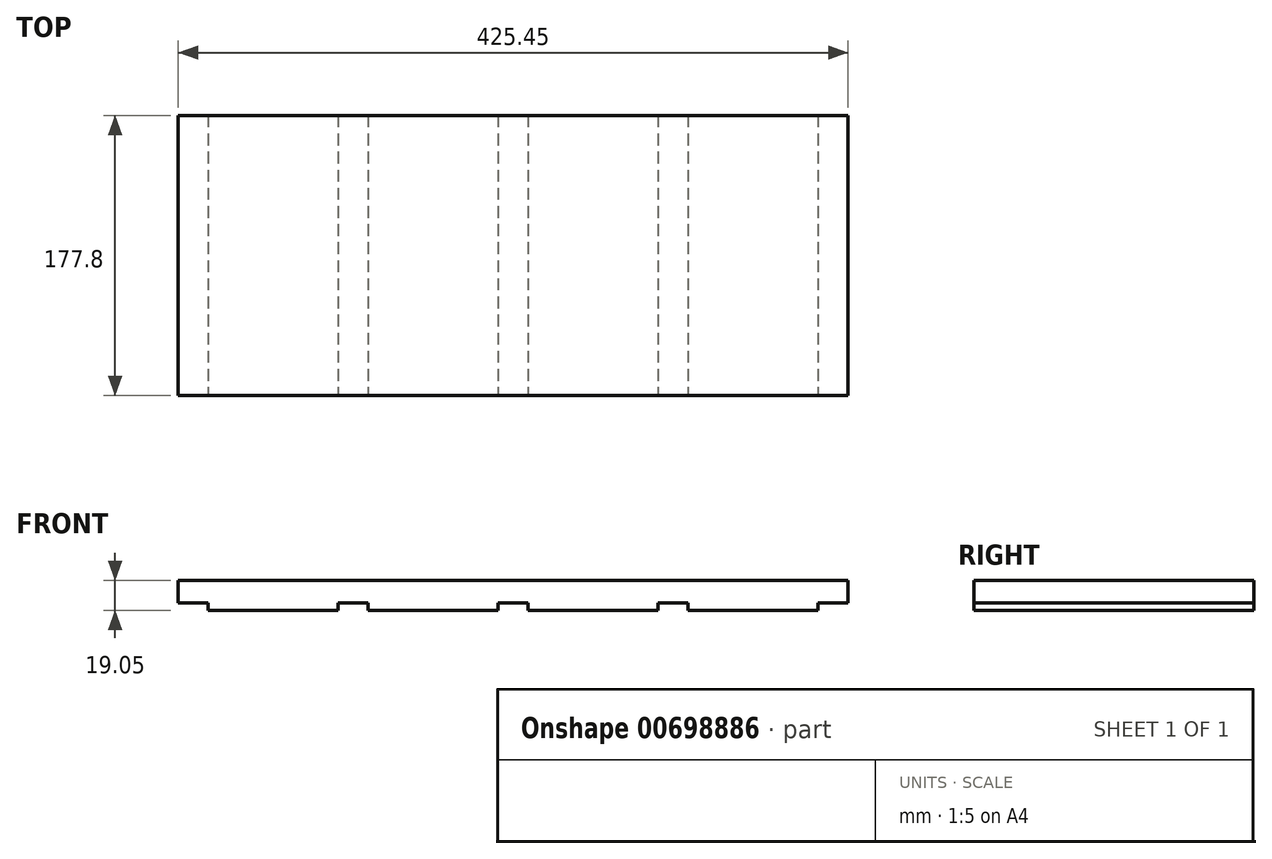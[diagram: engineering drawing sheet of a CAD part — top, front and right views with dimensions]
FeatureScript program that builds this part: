
annotation { "Feature Type Name" : "Feature", "Feature Type Description" : "" }
export const myFeature = defineFeature(function(context is Context, id is Id, definition is map)
    precondition{}
    {
        {
            var Q0;
            Q0=qCreatedBy(makeId("Front.planeOp"),FACE);
            var sketch = newSketch(context, id + "F0", { "sketchPlane" : qUnion([Q0])});
            skLineSegment(sketch, "E0.bottom", {"start": v(0, 0) * mm, "end": v(425.45, 0) * mm});
            skLineSegment(sketch, "E0.top", {"start": v(0, 19.05) * mm, "end": v(425.45, 19.05) * mm});
            skLineSegment(sketch, "E0.left", {"start": v(0, 0) * mm, "end": v(0, 19.05) * mm});
            skLineSegment(sketch, "E0.right", {"start": v(425.45, 0) * mm, "end": v(425.45, 19.05) * mm});
            skSolve(sketch);
        }
        {
            var Q0;
            Q0=qCreatedBy(makeId("Front.planeOp"),FACE);
            var sketch = newSketch(context, id + "F1", { "sketchPlane" : qUnion([Q0])});
            skLineSegment(sketch, "E1.bottom", {"start": v(101.6, 0) * mm, "end": v(120.65, 0) * mm});
            skLineSegment(sketch, "E1.top", {"start": v(101.6, 4.76) * mm, "end": v(120.65, 4.76) * mm});
            skLineSegment(sketch, "E1.left", {"start": v(101.6, 0) * mm, "end": v(101.6, 4.76) * mm});
            skLineSegment(sketch, "E1.right", {"start": v(120.65, 0) * mm, "end": v(120.65, 4.76) * mm});
            skLineSegment(sketch, "E2.1.0.0", {"start": v(203.2, 0) * mm, "end": v(222.25, 0) * mm});
            skLineSegment(sketch, "E2.1.0.1", {"start": v(203.2, 4.76) * mm, "end": v(222.25, 4.76) * mm});
            skLineSegment(sketch, "E2.1.0.2", {"start": v(203.2, 0) * mm, "end": v(203.2, 4.76) * mm});
            skLineSegment(sketch, "E2.1.0.3", {"start": v(222.25, 0) * mm, "end": v(222.25, 4.76) * mm});
            skLineSegment(sketch, "E2.2.0.0", {"start": v(304.8, 0) * mm, "end": v(323.85, 0) * mm});
            skLineSegment(sketch, "E2.2.0.1", {"start": v(304.8, 4.76) * mm, "end": v(323.85, 4.76) * mm});
            skLineSegment(sketch, "E2.2.0.2", {"start": v(304.8, 0) * mm, "end": v(304.8, 4.76) * mm});
            skLineSegment(sketch, "E2.2.0.3", {"start": v(323.85, 0) * mm, "end": v(323.85, 4.76) * mm});
            skLineSegment(sketch, "E2.direction1", {"start": v(101.6, 0) * mm, "end": v(203.2, 0) * mm, "construction": true});
            skLineSegment(sketch, "E3.0.3.0", {"start": v(406.4, 0) * mm, "end": v(425.45, 0) * mm});
            skLineSegment(sketch, "E3.3.3.0", {"start": v(406.4, 4.76) * mm, "end": v(425.45, 4.76) * mm});
            skLineSegment(sketch, "E3.6.3.0", {"start": v(406.4, 0) * mm, "end": v(406.4, 4.76) * mm});
            skLineSegment(sketch, "E3.9.3.0", {"start": v(425.45, 0) * mm, "end": v(425.45, 4.76) * mm});
            skLineSegment(sketch, "E4.bottom", {"start": v(0, 0) * mm, "end": v(19.05, 0) * mm});
            skLineSegment(sketch, "E4.top", {"start": v(0, 4.76) * mm, "end": v(19.05, 4.76) * mm});
            skLineSegment(sketch, "E4.left", {"start": v(0, 0) * mm, "end": v(0, 4.76) * mm});
            skLineSegment(sketch, "E4.right", {"start": v(19.05, 0) * mm, "end": v(19.05, 4.76) * mm});
            skSolve(sketch);
        }
        {
            var Q0;
            Q0=qSketchRegion(id+"F0",true);
            extrude(context, id + "F2", {"entities" : qUnion([Q0]), "oppositeDirection" : true, "depth" : 177.8 * mm, "offsetDistance" : 25.4 * mm});
        }
        {
            var Q0;
            Q0=qSketchRegion(id+"F1",true);
            extrude(context, id + "F3", {"entities" : qUnion([Q0]), "operationType" : NewBodyOperationType.REMOVE, "endBound" : BoundingType.THROUGH_ALL, "oppositeDirection" : true, "depth" : 25.4 * mm, "offsetDistance" : 25.4 * mm});
        }
    });
